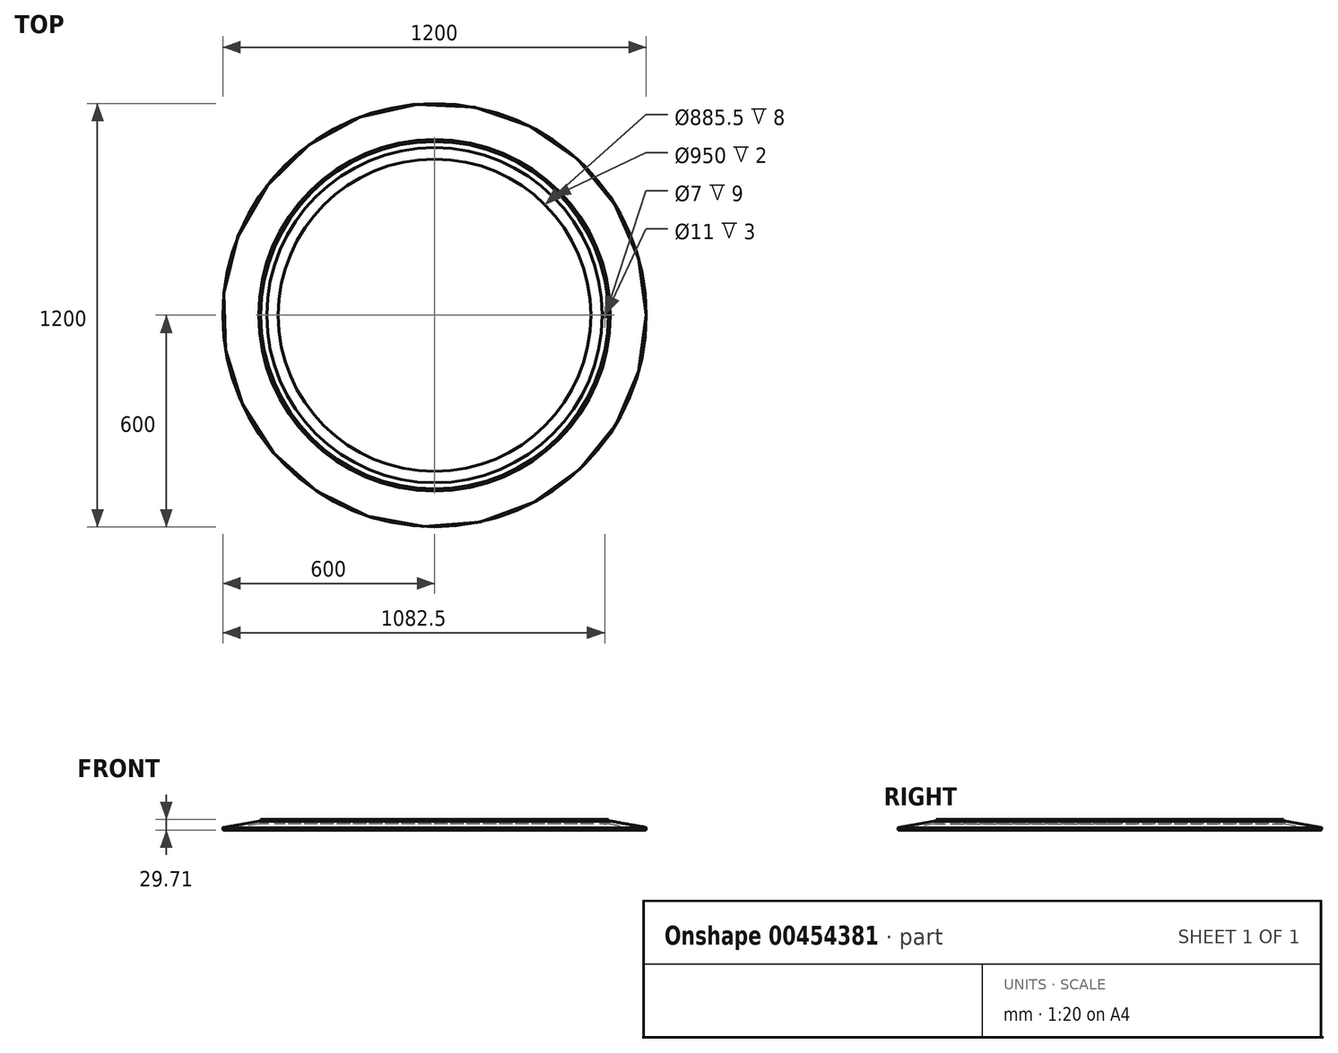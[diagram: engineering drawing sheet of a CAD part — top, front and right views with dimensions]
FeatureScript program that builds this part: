
annotation { "Feature Type Name" : "Feature", "Feature Type Description" : "" }
export const myFeature = defineFeature(function(context is Context, id is Id, definition is map)
    precondition{}
    {
        {
            var Q0;
            Q0=qCreatedBy(makeId("Front.planeOp"),FACE);
            var sketch = newSketch(context, id + "F0", { "sketchPlane" : qUnion([Q0])});
            skLineSegment(sketch, "E0", {"start": v(-475, 0) * mm, "end": v(-492.5, 0) * mm});
            skLineSegment(sketch, "E1", {"start": v(0, 0) * mm, "end": v(0, -404.95) * mm});
            skLineSegment(sketch, "E2", {"start": v(-475, 0) * mm, "end": v(-475, -4) * mm});
            skLineSegment(sketch, "E3", {"start": v(-496.78, -12) * mm, "end": v(-442.75, -12) * mm});
            skLineSegment(sketch, "E4", {"start": v(-475, -4) * mm, "end": v(-442.75, -4) * mm});
            skLineSegment(sketch, "E5.trimOffspring", {"start": v(-442.75, -4) * mm, "end": v(-442.75, -12) * mm});
            skLineSegment(sketch, "E6", {"start": v(-492.5, 0) * mm, "end": v(-492.5, -4) * mm});
            skLineSegment(sketch, "E7", {"start": v(-597.07, -29.68) * mm, "end": v(-496.78, -12) * mm});
            skLineSegment(sketch, "E8.0", {"start": v(-598.35, -21.79) * mm, "end": v(-498.17, -4.12) * mm});
            skPoint(sketch, "E9.visualSharp", {"position": v(-597.05, -21.56) * mm});
            skPoint(sketch, "E10.visualSharp", {"position": v(-595.66, -29.43) * mm});
            skArc(sketch, "E11", {"start": v(-598.35, -21.79) * mm, "mid": v(-599.64, -22.6) * mm, "end": v(-599.97, -24.1) * mm});
            skLineSegment(sketch, "E12", {"start": v(-599.97, -24.1) * mm, "end": v(-599.4, -28) * mm});
            skLineSegment(sketch, "E13.0", {"start": v(-597.7, -25.73) * mm, "end": v(-597.7, -25.73) * mm});
            skArc(sketch, "E14", {"start": v(-599.4, -28) * mm, "mid": v(-598.59, -29.34) * mm, "end": v(-597.07, -29.68) * mm});
            skLineSegment(sketch, "E15", {"start": v(-498.17, -4.12) * mm, "end": v(-492.5, -4) * mm});
            skSolve(sketch);
        }
        {
            var Q0;
            Q0 = qSketchRegion(id + "F0", true);
            var Q1;
            Q1=sQuery(id+"F0.wireOp",EDGE,"E1");
            revolve(context, id + "F1", {"entities" : qUnion([Q0]), "axis" : qUnion([Q1]), "revolveType" : RevolveType.FULL});
        }
        {
            var Q0;
            Q0=makeQuery(id+"F1.opRevolve","SWEPT_EDGE",EDGE,{"disambiguationData":[OSD([sQuery(id+"F0.wireOp",EDGE,"E2"),sQuery(id+"F0.wireOp",EDGE,"E4")])]});
            fillet(context, id + "F2", {"entities" : qUnion([Q0]), "radius" : 2 * mm, "tangentPropagation" : true, "allowEdgeOverflow" : false});
        }
        {
            var Q0;
            Q0=makeQuery(id+"F1.opRevolve","SWEPT_EDGE",EDGE,{"disambiguationData":[OSD([sQuery(id+"F0.wireOp",EDGE,"E6"),sQuery(id+"F0.wireOp",EDGE,"E15")])]});
            fillet(context, id + "F3", {"entities" : qUnion([Q0]), "radius" : 2 * mm, "tangentPropagation" : true, "allowEdgeOverflow" : false});
        }
        {
            var Q0;
            Q0=makeQuery(id+"F1.opRevolve","SWEPT_FACE",FACE,{"disambiguationData":[OSD([sQuery(id+"F0.wireOp",EDGE,"E0")])]});
            var sketch = newSketch(context, id + "F4", { "sketchPlane" : qUnion([Q0])});
            skPoint(sketch, "E16", {"position": v(482.5, 0) * mm});
            skSolve(sketch);
        }
        {
            var Q0;
            Q0=sQuery(id+"F4.wireOp",VERTEX,"E16");
            var Q1;
            Q1=makeQuery(id+"F1.opRevolve","SWEPT_BODY",BODY,{"disambiguationData":[OSD([sQuery(id+"F0.wireOp",EDGE,"E0"),sQuery(id+"F0.wireOp",EDGE,"E2"),sQuery(id+"F0.wireOp",EDGE,"E3"),sQuery(id+"F0.wireOp",EDGE,"E4"),sQuery(id+"F0.wireOp",EDGE,"E5.trimOffspring"),sQuery(id+"F0.wireOp",EDGE,"E6"),sQuery(id+"F0.wireOp",EDGE,"E7"),sQuery(id+"F0.wireOp",EDGE,"E8.0"),sQuery(id+"F0.wireOp",EDGE,"E11"),sQuery(id+"F0.wireOp",EDGE,"E12"),sQuery(id+"F0.wireOp",EDGE,"E14"),sQuery(id+"F0.wireOp",EDGE,"E15")])]});
            hole(context, id + "F5", {"style" : HoleStyle.C_BORE, "endStyle" : HoleEndStyle.THROUGH, "holeDiameter" : 7 * mm, "cBoreDiameter" : 11 * mm, "cBoreDepth" : 3 * mm, "isTappedThrough" : true, "tappedDepth" : 12 * mm, "tapClearance" : 3, "locations" : qUnion([Q0]), "scope" : qUnion([Q1])});
        }
    });
